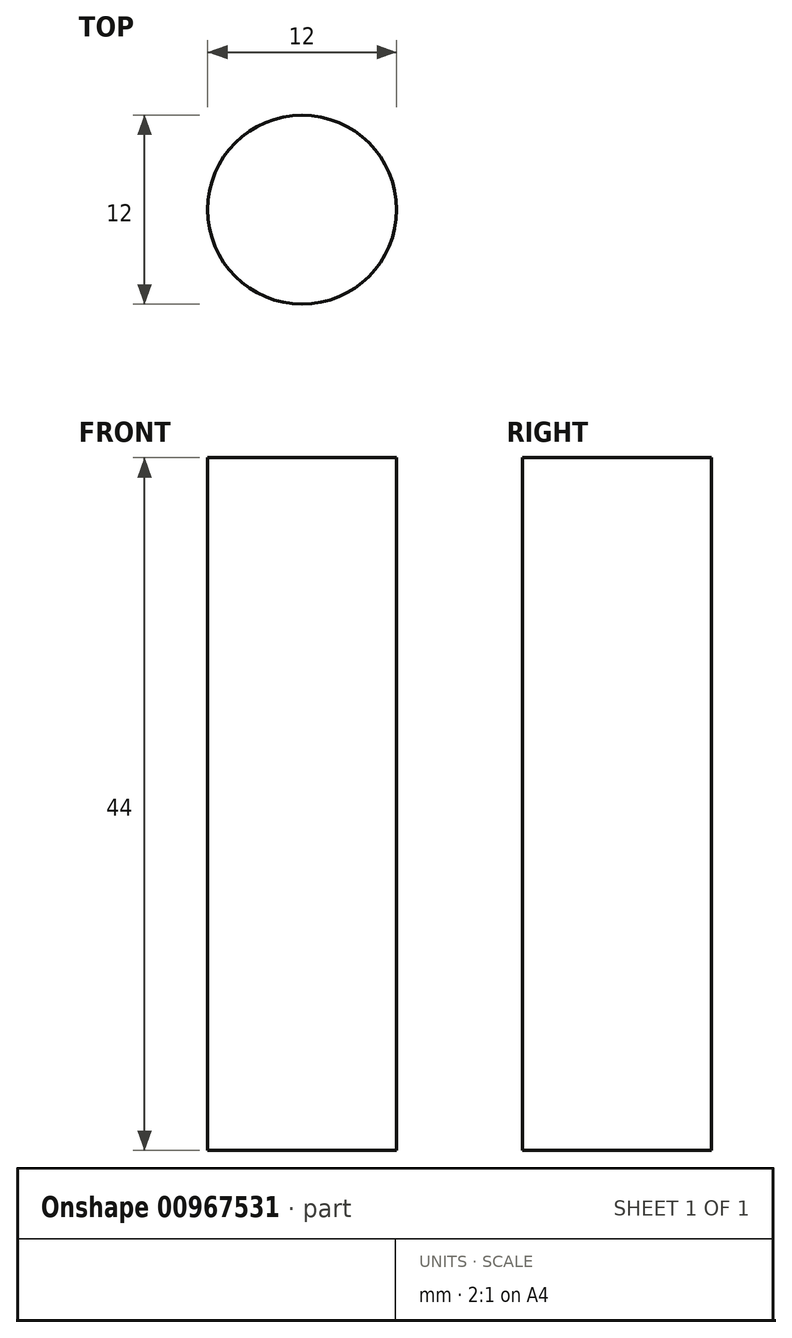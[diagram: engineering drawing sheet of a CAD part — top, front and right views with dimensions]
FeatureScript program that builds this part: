
annotation { "Feature Type Name" : "Feature", "Feature Type Description" : "" }
export const myFeature = defineFeature(function(context is Context, id is Id, definition is map)
    precondition{}
    {
        {
            var Q0;
            Q0=qCreatedBy(makeId("Top.planeOp"),FACE);
            var sketch = newSketch(context, id + "F0", { "sketchPlane" : qUnion([Q0])});
            skCircle(sketch, "E0", {"center": v(0, 0) * mm, "radius": 6 * mm});
            skSolve(sketch);
        }
        {
            var Q0;
            Q0=makeQuery(id+"F0.imprint","IMPRINT",FACE,{"disambiguationData":[TD([[makeQuery(id+"F0.imprint","IMPRINT",EDGE,{"derivedFrom":sQuery(id+"F0.wireOp",EDGE,"E0")}),1.0]])]});
            extrude(context, id + "F1", {"entities" : qUnion([Q0]), "depth" : 44 * mm, "offsetDistance" : 25 * mm, "symmetric" : true});
        }
    });
